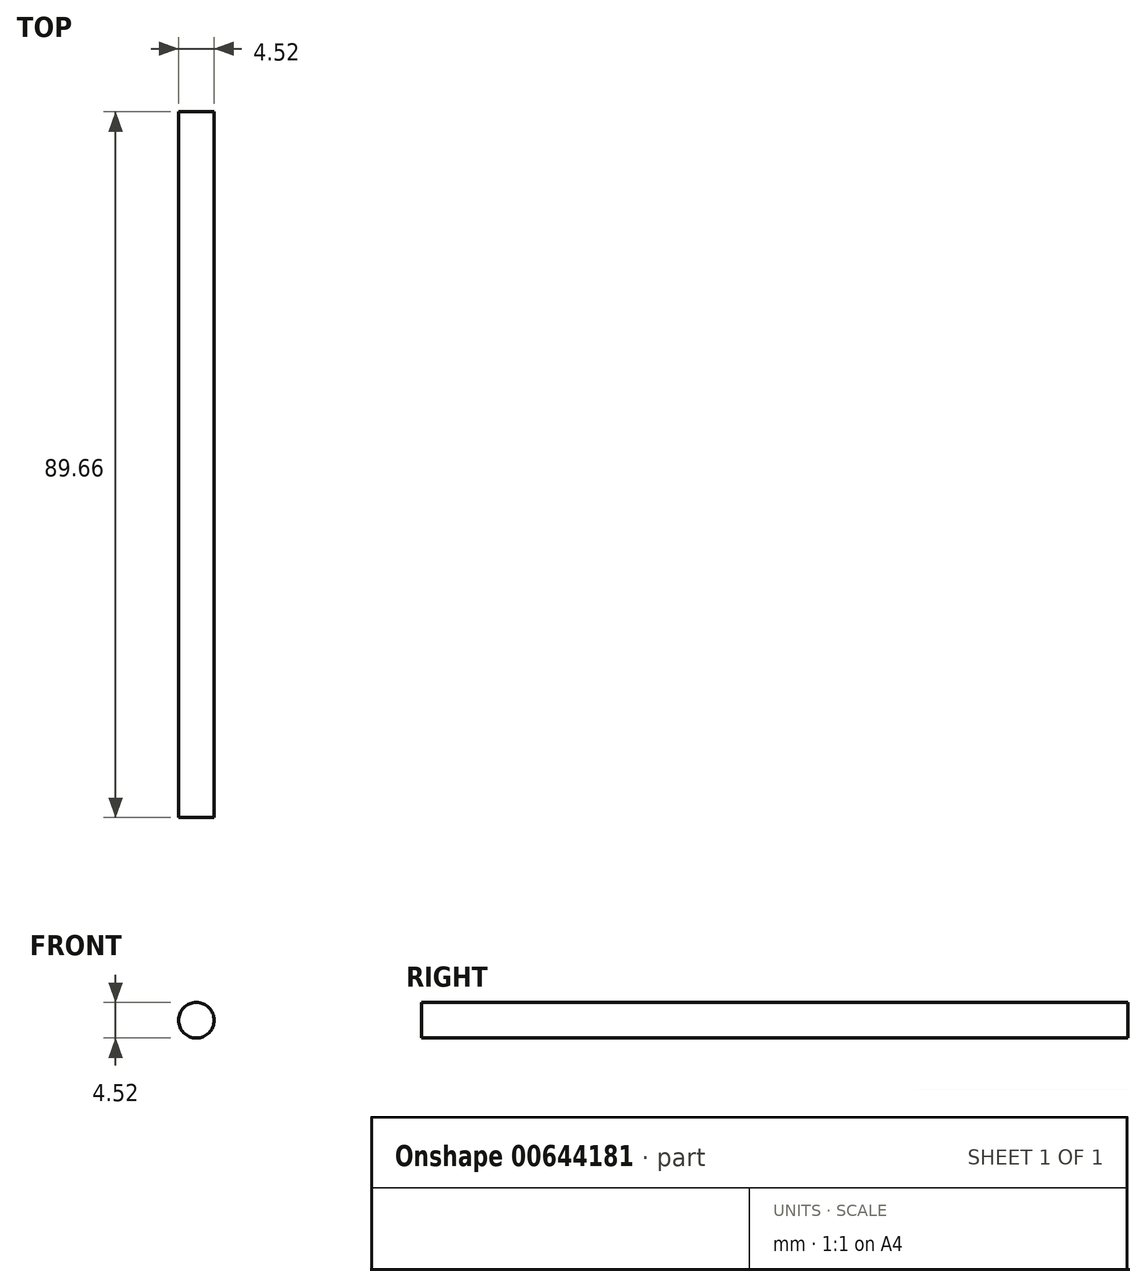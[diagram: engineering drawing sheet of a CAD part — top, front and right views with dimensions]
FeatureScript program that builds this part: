
annotation { "Feature Type Name" : "Feature", "Feature Type Description" : "" }
export const myFeature = defineFeature(function(context is Context, id is Id, definition is map)
    precondition{}
    {
        {
            var Q0;
            Q0=qCreatedBy(makeId("Front.planeOp"),FACE);
            var sketch = newSketch(context, id + "F0", { "sketchPlane" : qUnion([Q0])});
            skCircle(sketch, "E0", {"center": v(0, 0) * mm, "radius": 2.26 * mm});
            skSolve(sketch);
        }
        {
            var Q0;
            Q0 = qSketchRegion(id + "F0", true);
            extrude(context, id + "F1", {"entities" : qUnion([Q0]), "depth" : 89.66 * mm, "offsetDistance" : 25.4 * mm});
        }
    });
